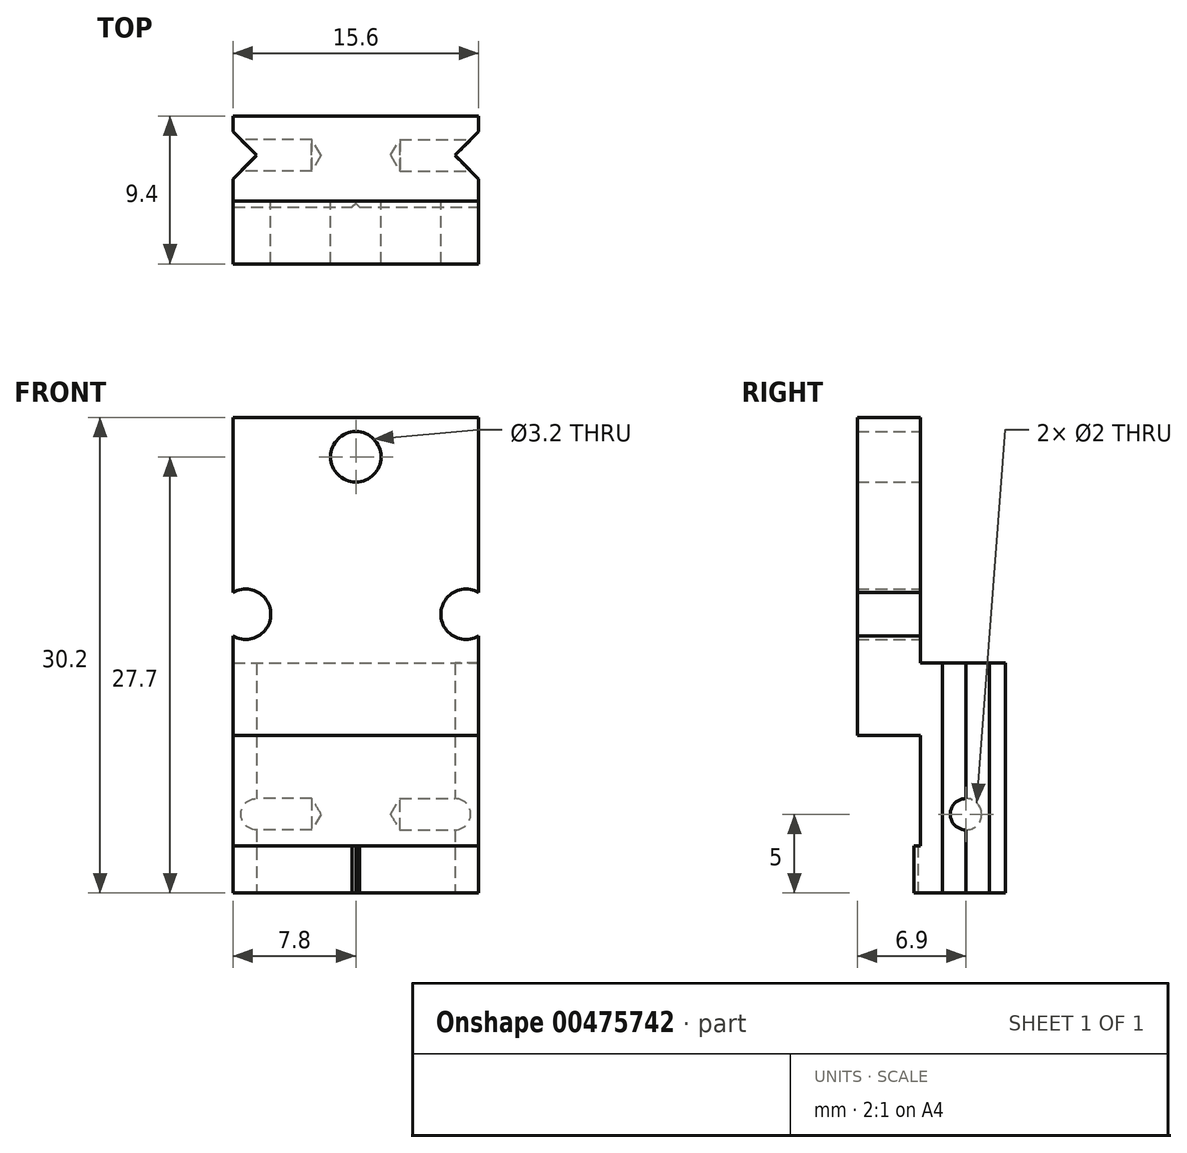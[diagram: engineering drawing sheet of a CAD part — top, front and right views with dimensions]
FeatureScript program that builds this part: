
annotation { "Feature Type Name" : "Feature", "Feature Type Description" : "" }
export const myFeature = defineFeature(function(context is Context, id is Id, definition is map)
    precondition{}
    {
        {
            var Q0;
            Q0=qCreatedBy(makeId("Front.planeOp"),FACE);
            var sketch = newSketch(context, id + "F0", { "sketchPlane" : qUnion([Q0])});
            skLineSegment(sketch, "E0.bottom", {"start": v(-7.8, 0) * mm, "end": v(7.8, 0) * mm});
            skLineSegment(sketch, "E0.top", {"start": v(-7.8, 20.2) * mm, "end": v(7.8, 20.2) * mm});
            skLineSegment(sketch, "E0.left", {"start": v(-7.8, 0) * mm, "end": v(-7.8, 20.2) * mm});
            skLineSegment(sketch, "E0.right", {"start": v(7.8, 0) * mm, "end": v(7.8, 20.2) * mm});
            skPoint(sketch, "E1", {"position": v(0, 0) * mm});
            skCircle(sketch, "E2", {"center": v(0, 17.7) * mm, "radius": 1.6 * mm});
            skCircle(sketch, "E3", {"center": v(-7, 7.7) * mm, "radius": 1.6 * mm});
            skCircle(sketch, "E4.MirrorC", {"center": v(7, 7.7) * mm, "radius": 1.6 * mm});
            skSolve(sketch);
        }
        {
            var Q0;
            {var subQ4=sQuery(id+"F0.wireOp",EDGE,"E0.bottom");Q0=makeQuery(id+"F0.imprint","IMPRINT",FACE,{"disambiguationData":[TD([[makeQuery(id+"F0.imprint","IMPRINT",EDGE,{"derivedFrom":subQ4}),1.0]])]});}
            extrude(context, id + "F1", {"entities" : qUnion([Q0]), "depth" : 4 * mm});
        }
        {
            var Q0;
            Q0=qCreatedBy(makeId("Front.planeOp"),FACE);
            var sketch = newSketch(context, id + "F2", { "sketchPlane" : qUnion([Q0])});
            skLineSegment(sketch, "E5.bottom", {"start": v(-7.8, 4.6) * mm, "end": v(7.8, 4.6) * mm});
            skLineSegment(sketch, "E5.top", {"start": v(-7.8, -10) * mm, "end": v(7.8, -10) * mm});
            skLineSegment(sketch, "E5.left", {"start": v(-7.8, 4.6) * mm, "end": v(-7.8, -10) * mm});
            skLineSegment(sketch, "E5.right", {"start": v(7.8, 4.6) * mm, "end": v(7.8, -10) * mm});
            skPoint(sketch, "E6", {"position": v(0, 4.6) * mm});
            skSolve(sketch);
        }
        {
            var Q0;
            Q0=makeQuery(id+"F2.imprint","IMPRINT",FACE,{"disambiguationData":[TD([[makeQuery(id+"F2.imprint","IMPRINT",EDGE,{"derivedFrom":sQuery(id+"F2.wireOp",EDGE,"E5.bottom")}),-1.0]])]});
            extrude(context, id + "F3", {"entities" : qUnion([Q0]), "operationType" : NewBodyOperationType.ADD, "oppositeDirection" : true, "depth" : 5.4 * mm});
        }
        {
            var Q0;
            Q0=makeQuery(id+"F3.opExtrude","CAP_FACE",FACE,{"disambiguationData":[OSD([sQuery(id+"F2.wireOp",EDGE,"E5.bottom"),sQuery(id+"F2.wireOp",EDGE,"E5.top"),sQuery(id+"F2.wireOp",EDGE,"E5.left"),sQuery(id+"F2.wireOp",EDGE,"E5.right")])],"isStart":true});
            var sketch = newSketch(context, id + "F4", { "sketchPlane" : qUnion([Q0])});
            skLineSegment(sketch, "E7.bottom", {"start": v(-7.8, -10) * mm, "end": v(7.8, -10) * mm});
            skLineSegment(sketch, "E7.top", {"start": v(-7.8, -7) * mm, "end": v(7.8, -7) * mm});
            skLineSegment(sketch, "E7.left", {"start": v(-7.8, -10) * mm, "end": v(-7.8, -7) * mm});
            skLineSegment(sketch, "E7.right", {"start": v(7.8, -10) * mm, "end": v(7.8, -7) * mm});
            skSolve(sketch);
        }
        {
            var Q0;
            Q0 = qSketchRegion(id + "F4", true);
            var Q1;
            Q1=makeQuery(id+"F4.imprint","IMPRINT",FACE,{"disambiguationData":[TD([[makeQuery(id+"F4.imprint","IMPRINT",EDGE,{"derivedFrom":sQuery(id+"F4.wireOp",EDGE,"E7.bottom")}),1.0]])]});
            extrude(context, id + "F5", {"entities" : qUnion([Q0, Q1]), "operationType" : NewBodyOperationType.ADD, "depth" : 0.4 * mm});
        }
        {
            var Q0;
            {var subQ0=sQuery(id+"F0.wireOp",EDGE,"E0.right");Q0=makeQuery(id+"F5.boolean.opBoolean","MERGE",FACE,{"derivedFrom":[makeQuery(id+"F3.boolean.opBoolean","MERGE",FACE,{"derivedFrom":[makeQuery(id+"F1.opExtrude","SWEPT_FACE",FACE,{"disambiguationData":[OSD([subQ0]),TDD([makeQuery(id+"F0.imprint","IMPRINT",EDGE,{"disambiguationData":[TD([[makeQuery(id+"F0.imprint","INTERSECT",VERTEX,{"derivedFrom":[sQuery(id+"F0.wireOp",EDGE,"E0.bottom"),subQ0]}),-1.0]])],"derivedFrom":subQ0})])]}),makeQuery(id+"F3.opExtrude","SWEPT_FACE",FACE,{"disambiguationData":[OSD([sQuery(id+"F2.wireOp",EDGE,"E5.right")])]})]}),makeQuery(id+"F5.opExtrude","SWEPT_FACE",FACE,{"disambiguationData":[OSD([sQuery(id+"F4.wireOp",EDGE,"E7.right")])]})]});}
            var sketch = newSketch(context, id + "F6", { "sketchPlane" : qUnion([Q0])});
            skPoint(sketch, "E8", {"position": v(2.9, -5) * mm});
            skSolve(sketch);
        }
        {
            var Q0;
            {var subQ0=sQuery(id+"F0.wireOp",EDGE,"E0.left");Q0=makeQuery(id+"F5.boolean.opBoolean","MERGE",FACE,{"derivedFrom":[makeQuery(id+"F3.boolean.opBoolean","MERGE",FACE,{"derivedFrom":[makeQuery(id+"F1.opExtrude","SWEPT_FACE",FACE,{"disambiguationData":[OSD([subQ0]),TDD([makeQuery(id+"F0.imprint","IMPRINT",EDGE,{"disambiguationData":[TD([[makeQuery(id+"F0.imprint","INTERSECT",VERTEX,{"derivedFrom":[sQuery(id+"F0.wireOp",EDGE,"E0.bottom"),subQ0]}),-1.0]])],"derivedFrom":subQ0})])]}),makeQuery(id+"F3.opExtrude","SWEPT_FACE",FACE,{"disambiguationData":[OSD([sQuery(id+"F2.wireOp",EDGE,"E5.left")])]})]}),makeQuery(id+"F5.opExtrude","SWEPT_FACE",FACE,{"disambiguationData":[OSD([sQuery(id+"F4.wireOp",EDGE,"E7.left")])]})]});}
            var sketch = newSketch(context, id + "F7", { "sketchPlane" : qUnion([Q0])});
            skPoint(sketch, "E9", {"position": v(-2.9, -5) * mm});
            skSolve(sketch);
        }
        {
            var Q0;
            Q0=sQuery(id+"F6.wireOp",VERTEX,"E8");
            var Q1;
            Q1=sQuery(id+"F7.wireOp",VERTEX,"E9");
            var Q2;
            Q2=makeQuery(id+"F1.opExtrude","SWEPT_BODY",BODY,{"disambiguationData":[OSD([sQuery(id+"F0.wireOp",EDGE,"E0.bottom"),sQuery(id+"F0.wireOp",EDGE,"E0.top"),sQuery(id+"F0.wireOp",EDGE,"E0.left"),sQuery(id+"F0.wireOp",EDGE,"E0.right"),sQuery(id+"F0.wireOp",EDGE,"E2"),sQuery(id+"F0.wireOp",EDGE,"E3"),sQuery(id+"F0.wireOp",EDGE,"E4.MirrorC")])]});
            hole(context, id + "F8", {"style" : HoleStyle.SIMPLE, "endStyle" : HoleEndStyle.BLIND, "holeDiameter" : 2 * mm, "holeDepth" : 5 * mm, "tappedDepth" : 12 * mm, "tapClearance" : 3, "locations" : qUnion([Q0, Q1]), "scope" : qUnion([Q2])});
        }
        {
            var Q0;
            Q0=makeQuery(id+"F3.opExtrude","SWEPT_FACE",FACE,{"disambiguationData":[OSD([sQuery(id+"F2.wireOp",EDGE,"E5.top")])]});
            var sketch = newSketch(context, id + "F9", { "sketchPlane" : qUnion([Q0])});
            skLineSegment(sketch, "E10", {"start": v(7.8, -1.4) * mm, "end": v(6.3, -2.9) * mm});
            skLineSegment(sketch, "E11", {"start": v(6.3, -2.9) * mm, "end": v(7.8, -4.4) * mm});
            skLineSegment(sketch, "E12", {"start": v(7.8, -2.9) * mm, "end": v(-7.8, -2.9) * mm, "construction": true});
            skLineSegment(sketch, "E13.MirrorCS", {"start": v(-7.8, -1.4) * mm, "end": v(-6.3, -2.9) * mm});
            skLineSegment(sketch, "E14.MirrorCS", {"start": v(-6.3, -2.9) * mm, "end": v(-7.8, -4.4) * mm});
            skSolve(sketch);
        }
        {
            var Q0;
            {var subQ0=sQuery(id+"F9.wireOp",EDGE,"E13.MirrorCS");Q0=makeQuery(id+"F9.imprint","IMPRINT",FACE,{"disambiguationData":[TD([[makeQuery(id+"F9.imprint","IMPRINT",EDGE,{"derivedFrom":subQ0}),-1.0]])]});}
            var Q1;
            {var subQ0=sQuery(id+"F9.wireOp",EDGE,"E10");Q1=makeQuery(id+"F9.imprint","IMPRINT",FACE,{"disambiguationData":[TD([[makeQuery(id+"F9.imprint","IMPRINT",EDGE,{"derivedFrom":subQ0}),1.0]])]});}
            extrude(context, id + "F10", {"entities" : qUnion([Q0, Q1]), "operationType" : NewBodyOperationType.REMOVE, "oppositeDirection" : true, "depth" : 25 * mm});
        }
        {
            var Q0;
            Q0=makeQuery(id+"F5.boolean.opBoolean","MERGE",FACE,{"derivedFrom":[makeQuery(id+"F3.opExtrude","SWEPT_FACE",FACE,{"disambiguationData":[OSD([sQuery(id+"F2.wireOp",EDGE,"E5.top")])]}),makeQuery(id+"F5.opExtrude","SWEPT_FACE",FACE,{"disambiguationData":[OSD([sQuery(id+"F4.wireOp",EDGE,"E7.bottom")])]})]});
            var sketch = newSketch(context, id + "F11", { "sketchPlane" : qUnion([Q0])});
            skLineSegment(sketch, "E15", {"start": v(0, 0.4) * mm, "end": v(0, -5.4) * mm, "construction": true});
            skLineSegment(sketch, "E16", {"start": v(0, 0.15) * mm, "end": v(0.25, 0.4) * mm});
            skLineSegment(sketch, "E17", {"start": v(0, 0.15) * mm, "end": v(-0.25, 0.4) * mm});
            skSolve(sketch);
        }
        {
            var Q0;
            {var subQ0=sQuery(id+"F11.wireOp",EDGE,"E16");Q0=makeQuery(id+"F11.imprint","IMPRINT",FACE,{"disambiguationData":[TD([[makeQuery(id+"F11.imprint","IMPRINT",EDGE,{"derivedFrom":subQ0}),1.0]])]});}
            extrude(context, id + "F12", {"entities" : qUnion([Q0]), "operationType" : NewBodyOperationType.REMOVE, "endBound" : BoundingType.UP_TO_NEXT, "oppositeDirection" : true, "depth" : 25 * mm});
        }
    });
